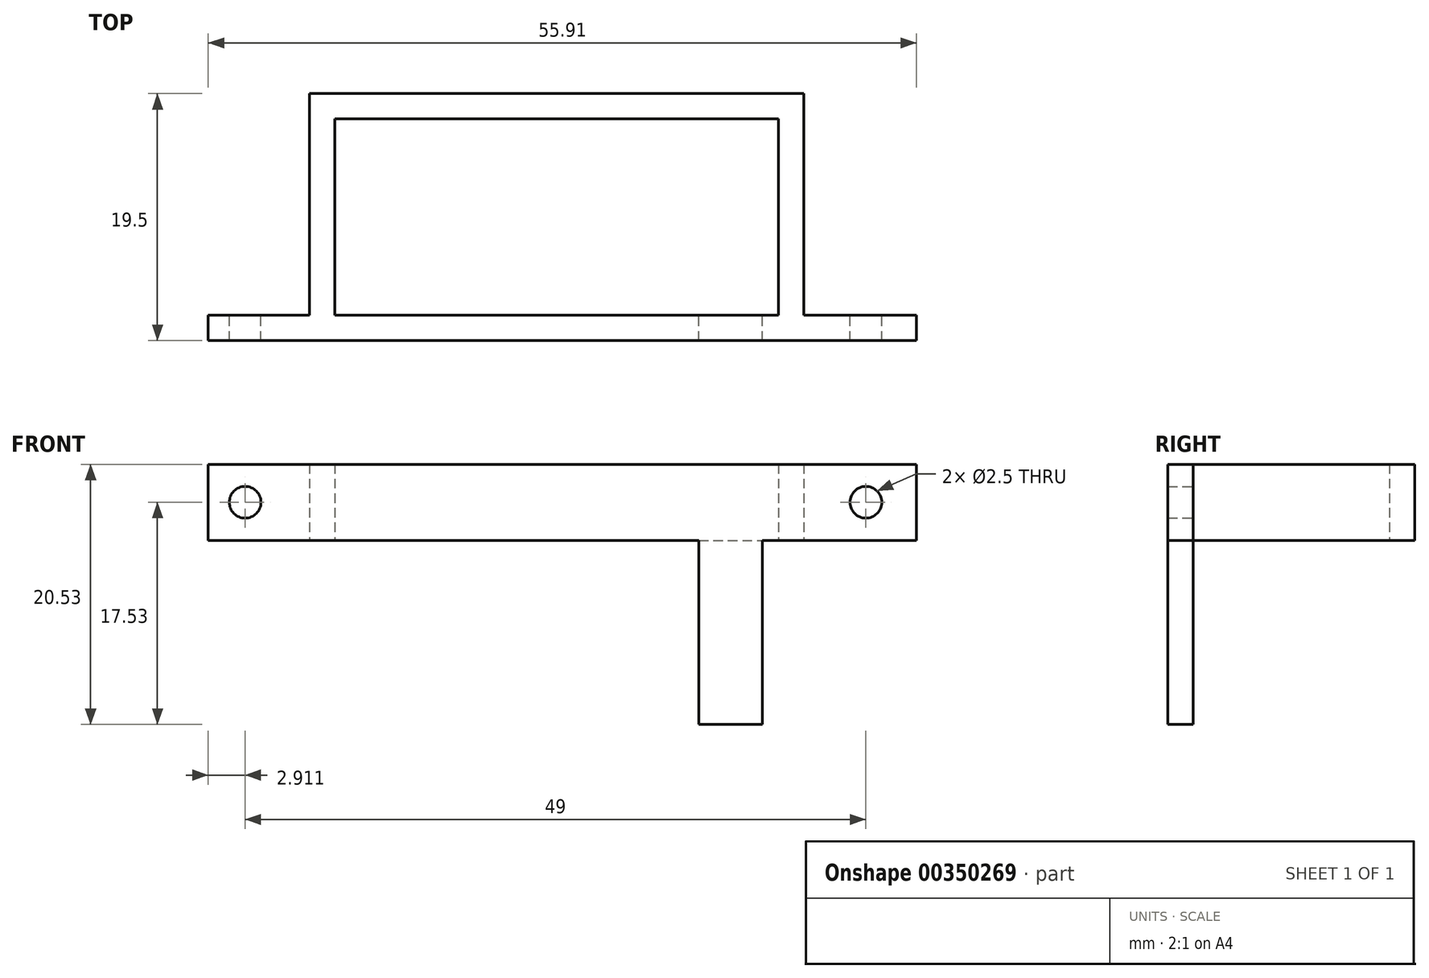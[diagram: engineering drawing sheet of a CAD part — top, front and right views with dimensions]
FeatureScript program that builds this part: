
annotation { "Feature Type Name" : "Feature", "Feature Type Description" : "" }
export const myFeature = defineFeature(function(context is Context, id is Id, definition is map)
    precondition{}
    {
        {
            var Q0;
            Q0=qCreatedBy(makeId("Top.planeOp"),FACE);
            var sketch = newSketch(context, id + "F0", { "sketchPlane" : qUnion([Q0])});
            skLineSegment(sketch, "E0.bottom", {"start": v(-57, 0) * mm, "end": v(-49, 0) * mm});
            skLineSegment(sketch, "E0.top", {"start": v(-57, -2) * mm, "end": v(-1.09, -2) * mm});
            skLineSegment(sketch, "E0.left", {"start": v(-57, 0) * mm, "end": v(-57, -2) * mm});
            skLineSegment(sketch, "E0.right", {"start": v(-1.09, 0) * mm, "end": v(-1.09, -2) * mm});
            skLineSegment(sketch, "E1", {"start": v(-49, 0) * mm, "end": v(-49, 17.5) * mm});
            skLineSegment(sketch, "E2.trimOffspring", {"start": v(-1.09, 0) * mm, "end": v(75.13, 0) * mm});
            skLineSegment(sketch, "E3", {"start": v(999.45, 0) * mm, "end": v(-10, 0) * mm});
            skLineSegment(sketch, "E4", {"start": v(-10, 17.5) * mm, "end": v(-10, 0) * mm});
            skLineSegment(sketch, "E5", {"start": v(-10, 0) * mm, "end": v(-1.09, 0) * mm});
            skLineSegment(sketch, "E6.bottom", {"start": v(-47, 0) * mm, "end": v(-12, 0) * mm});
            skLineSegment(sketch, "E6.top", {"start": v(-47, 15.5) * mm, "end": v(-12, 15.5) * mm});
            skLineSegment(sketch, "E6.left", {"start": v(-47, 0) * mm, "end": v(-47, 15.5) * mm});
            skLineSegment(sketch, "E6.right", {"start": v(-12, 0) * mm, "end": v(-12, 15.5) * mm});
            skLineSegment(sketch, "E7", {"start": v(-10, 17.5) * mm, "end": v(-49, 17.5) * mm});
            skSolve(sketch);
        }
        {
            var Q0;
            Q0=qSketchRegion(id+"F0",true);
            var Q1;
            Q1=qSketchRegion(id+"F96PT0ErqWhOYXY_1",true);
            extrude(context, id + "F1", {"entities" : qUnion([Q0, Q1]), "endBound" : BoundingType.SYMMETRIC, "depth" : 6 * mm});
        }
        {
            var Q0;
            Q0=makeQuery(id+"F1.opExtrude","SWEPT_FACE",FACE,{"disambiguationData":[OSD([sQuery(id+"F0.wireOp",EDGE,"E0.top")])]});
            var sketch = newSketch(context, id + "F2", { "sketchPlane" : qUnion([Q0])});
            skCircle(sketch, "E8", {"center": v(-5.09, 0) * mm, "radius": 1.25 * mm});
            skCircle(sketch, "E9", {"center": v(-54.09, 0) * mm, "radius": 1.25 * mm});
            skSolve(sketch);
        }
        {
            var Q0;
            Q0=makeQuery(id+"F2.imprint","IMPRINT",FACE,{"disambiguationData":[TD([[makeQuery(id+"F2.imprint","IMPRINT",EDGE,{"derivedFrom":sQuery(id+"F2.wireOp",EDGE,"E9")}),1.0]])]});
            var Q1;
            Q1=makeQuery(id+"F2.imprint","IMPRINT",FACE,{"disambiguationData":[TD([[makeQuery(id+"F2.imprint","IMPRINT",EDGE,{"derivedFrom":sQuery(id+"F2.wireOp",EDGE,"E8")}),1.0]])]});
            extrude(context, id + "F3", {"entities" : qUnion([Q0, Q1]), "operationType" : NewBodyOperationType.REMOVE, "endBound" : BoundingType.SYMMETRIC, "depth" : 25 * mm});
        }
        {
            var Q0;
            Q0=qCreatedBy(makeId("Front.planeOp"),FACE);
            var sketch = newSketch(context, id + "F4", { "sketchPlane" : qUnion([Q0])});
            skLineSegment(sketch, "E10.bottom", {"start": v(-13.28, -2.69) * mm, "end": v(-18.28, -2.69) * mm});
            skLineSegment(sketch, "E10.top", {"start": v(-13.28, -17.53) * mm, "end": v(-18.28, -17.53) * mm});
            skLineSegment(sketch, "E10.left", {"start": v(-13.28, -2.69) * mm, "end": v(-13.28, -17.53) * mm});
            skLineSegment(sketch, "E10.right", {"start": v(-18.28, -2.69) * mm, "end": v(-18.28, -17.53) * mm});
            skLineSegment(sketch, "E11.bottom", {"start": v(-18.28, -2.69) * mm, "end": v(-18.28, -3.86) * mm});
            skSolve(sketch);
        }
        {
            var Q0;
            Q0=makeQuery(id+"F4.imprint","IMPRINT",FACE,{"disambiguationData":[TD([[makeQuery(id+"F4.imprint","IMPRINT",EDGE,{"derivedFrom":sQuery(id+"F4.wireOp",EDGE,"E10.bottom")}),1.0]])]});
            extrude(context, id + "F5", {"entities" : qUnion([Q0]), "operationType" : NewBodyOperationType.ADD, "depth" : 2 * mm});
        }
    });
